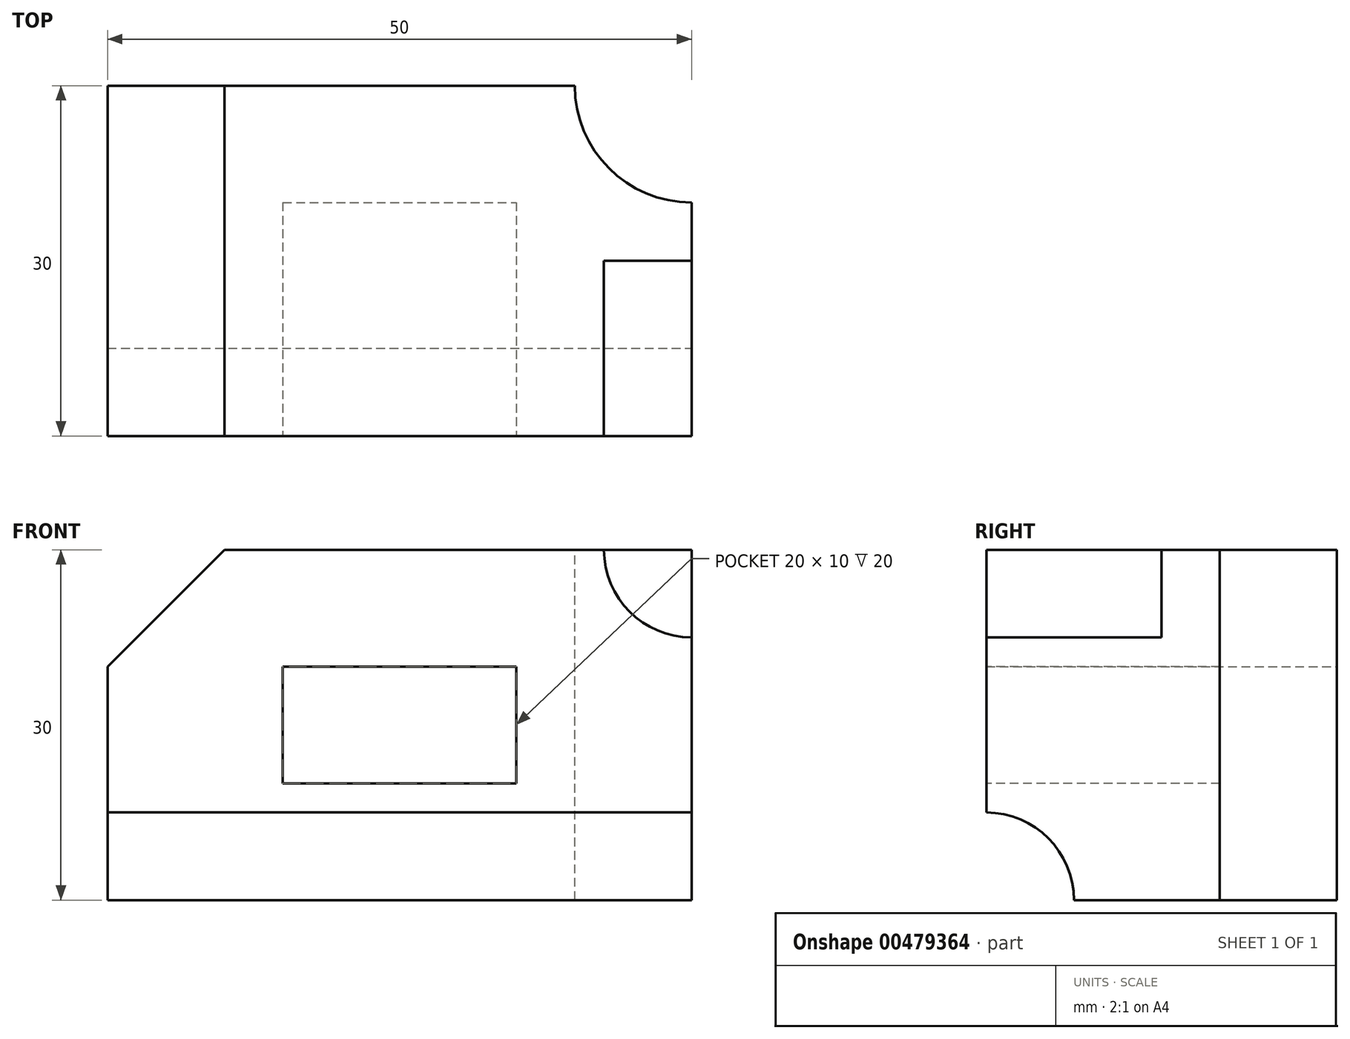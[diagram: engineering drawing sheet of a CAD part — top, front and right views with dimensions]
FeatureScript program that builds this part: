
annotation { "Feature Type Name" : "Feature", "Feature Type Description" : "" }
export const myFeature = defineFeature(function(context is Context, id is Id, definition is map)
    precondition{}
    {
        {
            var Q0;
            Q0=qCreatedBy(makeId("Top.planeOp"),FACE);
            var sketch = newSketch(context, id + "F0", { "sketchPlane" : qUnion([Q0])});
            skLineSegment(sketch, "E0.bottom", {"start": v(0, 0) * mm, "end": v(50, 0) * mm});
            skLineSegment(sketch, "E0.top", {"start": v(0, 30) * mm, "end": v(50, 30) * mm});
            skLineSegment(sketch, "E0.left", {"start": v(0, 0) * mm, "end": v(0, 30) * mm});
            skLineSegment(sketch, "E0.right", {"start": v(50, 0) * mm, "end": v(50, 30) * mm});
            skSolve(sketch);
        }
        {
            var Q0;
            Q0 = qSketchRegion(id + "F0", true);
            extrude(context, id + "F1", {"entities" : qUnion([Q0]), "depth" : 30 * mm});
        }
        {
            var Q0;
            Q0=makeQuery(id+"F1.opExtrude","SWEPT_FACE",FACE,{"disambiguationData":[OSD([sQuery(id+"F0.wireOp",EDGE,"E0.right")])]});
            var sketch = newSketch(context, id + "F2", { "sketchPlane" : qUnion([Q0])});
            skCircle(sketch, "E1", {"center": v(0, 0) * mm, "radius": 7.5 * mm});
            skSolve(sketch);
        }
        {
            var Q0;
            Q0 = qSketchRegion(id + "F2", true);
            extrude(context, id + "F3", {"entities" : qUnion([Q0]), "operationType" : NewBodyOperationType.REMOVE, "endBound" : BoundingType.THROUGH_ALL, "oppositeDirection" : true, "depth" : 25 * mm});
        }
        {
            var Q0;
            Q0=makeQuery(id+"F1.opExtrude","CAP_FACE",FACE,{"disambiguationData":[OSD([sQuery(id+"F0.wireOp",EDGE,"E0.bottom"),sQuery(id+"F0.wireOp",EDGE,"E0.top"),sQuery(id+"F0.wireOp",EDGE,"E0.left"),sQuery(id+"F0.wireOp",EDGE,"E0.right")])],"isStart":false});
            var sketch = newSketch(context, id + "F4", { "sketchPlane" : qUnion([Q0])});
            skCircle(sketch, "E2", {"center": v(50, 30) * mm, "radius": 10 * mm});
            skSolve(sketch);
        }
        {
            var Q0;
            Q0 = qSketchRegion(id + "F4", true);
            extrude(context, id + "F5", {"entities" : qUnion([Q0]), "operationType" : NewBodyOperationType.REMOVE, "endBound" : BoundingType.THROUGH_ALL, "oppositeDirection" : true, "depth" : 25 * mm});
        }
        {
            var Q0;
            Q0=makeQuery(id+"F1.opExtrude","SWEPT_FACE",FACE,{"disambiguationData":[OSD([sQuery(id+"F0.wireOp",EDGE,"E0.bottom")])]});
            var sketch = newSketch(context, id + "F6", { "sketchPlane" : qUnion([Q0])});
            skCircle(sketch, "E3", {"center": v(50, 30) * mm, "radius": 7.5 * mm});
            skSolve(sketch);
        }
        {
            var Q0;
            Q0 = qSketchRegion(id + "F6", true);
            extrude(context, id + "F7", {"entities" : qUnion([Q0]), "operationType" : NewBodyOperationType.REMOVE, "oppositeDirection" : true, "depth" : 15 * mm});
        }
        {
            var Q0;
            Q0=makeQuery(id+"F1.opExtrude","SWEPT_FACE",FACE,{"disambiguationData":[OSD([sQuery(id+"F0.wireOp",EDGE,"E0.bottom")])]});
            var sketch = newSketch(context, id + "F8", { "sketchPlane" : qUnion([Q0])});
            skLineSegment(sketch, "E4.bottom", {"start": v(15, 10) * mm, "end": v(35, 10) * mm});
            skLineSegment(sketch, "E4.top", {"start": v(15, 20) * mm, "end": v(35, 20) * mm});
            skLineSegment(sketch, "E4.left", {"start": v(15, 10) * mm, "end": v(15, 20) * mm});
            skLineSegment(sketch, "E4.right", {"start": v(35, 10) * mm, "end": v(35, 20) * mm});
            skSolve(sketch);
        }
        {
            var Q0;
            Q0 = qSketchRegion(id + "F8", true);
            extrude(context, id + "F9", {"entities" : qUnion([Q0]), "operationType" : NewBodyOperationType.REMOVE, "oppositeDirection" : true, "depth" : 20 * mm});
        }
        {
            var Q0;
            Q0=makeQuery(id+"F1.opExtrude","CAP_EDGE",EDGE,{"disambiguationData":[OSD([sQuery(id+"F0.wireOp",EDGE,"E0.left")])],"isStart":false});
            chamfer(context, id + "F10", {"entities" : qUnion([Q0]), "width" : 10 * mm, "tangentPropagation" : true});
        }
    });
